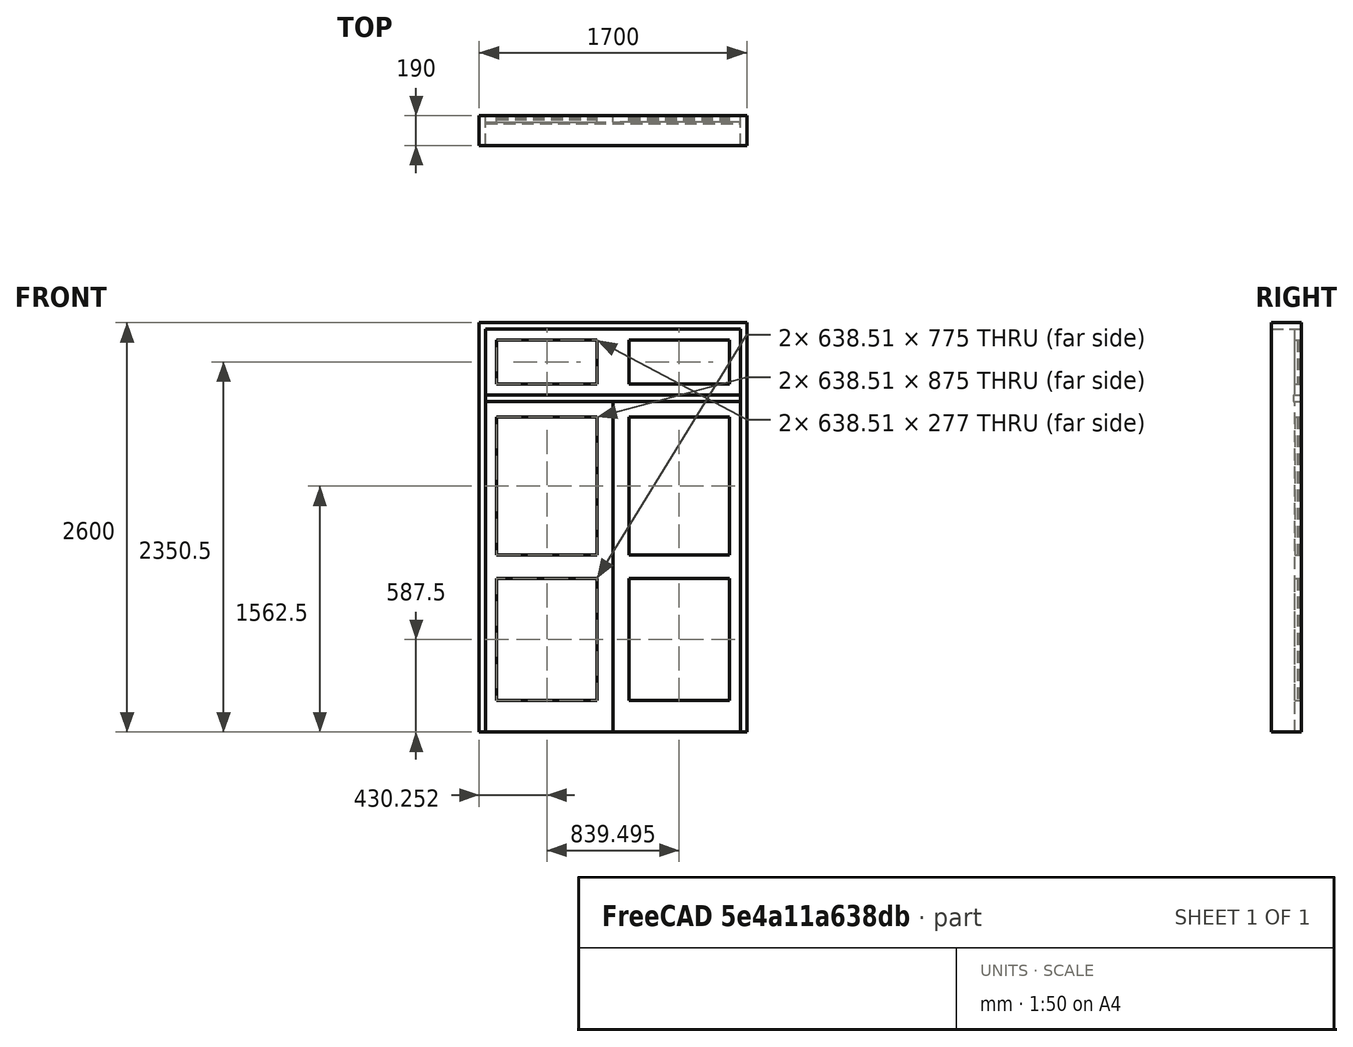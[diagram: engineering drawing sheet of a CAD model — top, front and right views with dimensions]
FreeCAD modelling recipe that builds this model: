
FCSTD DOCUMENT  (FreeCAD 0.16R6704 (Git))
Label: Double doors with glass and transom
License: CreativeCommons Attribution
LicenseURL: http://creativecommons.org/licenses/by/4.0/
objects: Sketcher::SketchObject×1, Part::FeaturePython×1
note: 2 computed .brp shape members not serialized (recipe doc carries the construction recipe); baked Part::Feature solids carry a one-line shape summary decoded from their .brp

FEATURE [Sketcher::SketchObject] Sketch179
  Placement = pos=(0,0,0) rot=(1,0,0;1.5708rad)
  sketch-geometry (50):
    g0: LineSegment StartX=0 StartY=0 StartZ=0 EndX=1700 EndY=0 EndZ=0
    g1: LineSegment StartX=1700 StartY=0 StartZ=0 EndX=1700 EndY=2600 EndZ=0
    g2: LineSegment StartX=1700 StartY=2600 StartZ=0 EndX=0 EndY=2600 EndZ=0
    g3: LineSegment StartX=0 StartY=2600 StartZ=0 EndX=0 EndY=0 EndZ=0
    g4: LineSegment StartX=40 StartY=0 StartZ=0 EndX=1660 EndY=0 EndZ=0
    g5: LineSegment StartX=1660 StartY=0 StartZ=0 EndX=1660 EndY=2560 EndZ=0
    g6: LineSegment StartX=1660 StartY=2560 StartZ=0 EndX=40 EndY=2560 EndZ=0
    g7: LineSegment StartX=40 StartY=2560 StartZ=0 EndX=40 EndY=0 EndZ=0
    g8: LineSegment StartX=111 StartY=2000 StartZ=0 EndX=749.505 EndY=2000 EndZ=0
    g9: LineSegment StartX=749.505 StartY=2000 StartZ=0 EndX=749.505 EndY=1125 EndZ=0
    g10: LineSegment StartX=749.505 StartY=1125 StartZ=0 EndX=111 EndY=1125 EndZ=0
    g11: LineSegment StartX=111 StartY=1125 StartZ=0 EndX=111 EndY=2000 EndZ=0
    g12: LineSegment StartX=111 StartY=975 StartZ=0 EndX=749.505 EndY=975 EndZ=0
    g13: LineSegment StartX=749.505 StartY=975 StartZ=0 EndX=749.505 EndY=200 EndZ=0
    g14: LineSegment StartX=749.505 StartY=200 StartZ=0 EndX=111 EndY=200 EndZ=0
    g15: LineSegment StartX=111 StartY=200 StartZ=0 EndX=111 EndY=975 EndZ=0
    g16: LineSegment [constr] StartX=-279.798 StartY=1050 StartZ=0 EndX=2204.66 EndY=1050 EndZ=0
    g17: LineSegment StartX=41 StartY=2100 StartZ=0 EndX=849.5 EndY=2100 EndZ=0
    g18: LineSegment StartX=849.5 StartY=2100 StartZ=0 EndX=849.5 EndY=1 EndZ=0
    g19: LineSegment StartX=849.5 StartY=1 StartZ=0 EndX=41 EndY=1 EndZ=0
    g20: LineSegment StartX=41 StartY=1 StartZ=0 EndX=41 EndY=2100 EndZ=0
    g21: LineSegment [constr] StartX=850 StartY=3136.34 StartZ=0 EndX=850 EndY=-186.521 EndZ=0
    g22: LineSegment StartX=1589 StartY=2000 StartZ=0 EndX=950.495 EndY=2000 EndZ=0
    g23: LineSegment StartX=950.495 StartY=2000 StartZ=0 EndX=950.495 EndY=1125 EndZ=0
    g24: LineSegment StartX=950.495 StartY=1125 StartZ=0 EndX=1589 EndY=1125 EndZ=0
    g25: LineSegment StartX=1589 StartY=1125 StartZ=0 EndX=1589 EndY=2000 EndZ=0
    g26: LineSegment StartX=1589 StartY=975 StartZ=0 EndX=950.495 EndY=975 EndZ=0
    g27: LineSegment StartX=950.495 StartY=975 StartZ=0 EndX=950.495 EndY=200 EndZ=0
    g28: LineSegment StartX=950.495 StartY=200 StartZ=0 EndX=1589 EndY=200 EndZ=0
    g29: LineSegment StartX=1589 StartY=200 StartZ=0 EndX=1589 EndY=975 EndZ=0
    g30: LineSegment StartX=1659 StartY=2100 StartZ=0 EndX=850.5 EndY=2100 EndZ=0
    g31: LineSegment StartX=850.5 StartY=2100 StartZ=0 EndX=850.5 EndY=1 EndZ=0
    g32: LineSegment StartX=850.5 StartY=1 StartZ=0 EndX=1659 EndY=1 EndZ=0
    g33: LineSegment StartX=1659 StartY=1 StartZ=0 EndX=1659 EndY=2100 EndZ=0
    g34: LineSegment StartX=41 StartY=2559 StartZ=0 EndX=1659 EndY=2559 EndZ=0
    g35: LineSegment StartX=1659 StartY=2559 StartZ=0 EndX=1659 EndY=2142 EndZ=0
    g36: LineSegment StartX=1659 StartY=2142 StartZ=0 EndX=41 EndY=2142 EndZ=0
    g37: LineSegment StartX=41 StartY=2142 StartZ=0 EndX=41 EndY=2559 EndZ=0
    g38: LineSegment StartX=111 StartY=2489 StartZ=0 EndX=749.505 EndY=2489 EndZ=0
    g39: LineSegment StartX=749.505 StartY=2489 StartZ=0 EndX=749.505 EndY=2212 EndZ=0
    g40: LineSegment StartX=749.505 StartY=2212 StartZ=0 EndX=111 EndY=2212 EndZ=0
    g41: LineSegment StartX=111 StartY=2212 StartZ=0 EndX=111 EndY=2489 EndZ=0
    g42: LineSegment StartX=950.495 StartY=2489 StartZ=0 EndX=1589 EndY=2489 EndZ=0
    g43: LineSegment StartX=1589 StartY=2489 StartZ=0 EndX=1589 EndY=2212 EndZ=0
    g44: LineSegment StartX=1589 StartY=2212 StartZ=0 EndX=950.495 EndY=2212 EndZ=0
    g45: LineSegment StartX=950.495 StartY=2212 StartZ=0 EndX=950.495 EndY=2489 EndZ=0
    g46: LineSegment StartX=41 StartY=2141 StartZ=0 EndX=1659 EndY=2141 EndZ=0
    g47: LineSegment StartX=1659 StartY=2141 StartZ=0 EndX=1659 EndY=2101 EndZ=0
    g48: LineSegment StartX=1659 StartY=2101 StartZ=0 EndX=41 EndY=2101 EndZ=0
    g49: LineSegment StartX=41 StartY=2101 StartZ=0 EndX=41 EndY=2141 EndZ=0
  constraints (143):
    c: Coincident(g0,g1)
    c: Coincident(g2,g3)
    c: Coincident(g3,g0)
    c: Horizontal(g0)
    c: Vertical(g1)
    c: Vertical(g3)
    c: Coincident(g4,g5)
    c: Coincident(g5,g6)
    c: Coincident(g6,g7)
    c: Coincident(g7,g4)
    c: Horizontal(g4)
    c: Horizontal(g6)
    c: Vertical(g5)
    c: Vertical(g7)
    c: DistanceY(g1) = 2600  'Altura do vão'
    c: DistanceX(g0) = 1700  'Largura do vão'
    c: DistanceY(g6,g2) = 40  'Altura batente superior'
    c: DistanceX(g2,g6) = 40  'Largura do batente 1'
    c: DistanceX(g4,g0) = 40  'Largura do batente 2'
    c: DistanceY(g0,g4) = 0  'Constraint21'
    c: Coincident(g0,g-1)
    c: Coincident(g8,g9)
    c: Coincident(g9,g10)
    c: Coincident(g10,g11)
    c: Coincident(g11,g8)
    c: Horizontal(g10)
    c: Vertical(g9)
    c: Vertical(g11)
    c: Coincident(g12,g13)
    c: Coincident(g13,g14)
    c: Coincident(g14,g15)
    c: Coincident(g15,g12)
    c: Horizontal(g12)
    c: Horizontal(g14)
    c: Vertical(g13)
    c: Vertical(g15)
    c: DistanceX(g9,g12) = 0
    c: DistanceY(g12,g10) = 150  'Altura do montante intermediário porta'
    c: DistanceY(g-1,g14) = 200  'Altura moldura inferior porta'
    c: DistanceY(g-1,g16) = 1050  'Altura da divisão intermediária porta'
    c: Coincident(g17,g18)  'Constraint46'
    c: Coincident(g18,g19)  'Constraint45'
    c: Coincident(g19,g20)  'Constraint43'
    c: Horizontal(g17)
    c: Horizontal(g19)
    c: Vertical(g18)
    c: Vertical(g20)
    c: DistanceY(g4,g18) = 1
    c: DistanceX(g6,g17) = 1
    c: Coincident(g22,g23)  'Constraint57'
    c: Coincident(g23,g24)  'Constraint55'
    c: Coincident(g24,g25)  'Constraint54'
    c: Coincident(g25,g22)
    c: Horizontal(g24)
    c: Vertical(g23)
    c: Vertical(g25)
    c: Coincident(g26,g27)
    c: Coincident(g27,g28)
    c: Coincident(g28,g29)
    c: Coincident(g29,g26)
    c: Horizontal(g26)
    c: Horizontal(g28)
    c: Vertical(g27)
    c: Vertical(g29)
    c: Coincident(g30,g31)
    c: Coincident(g31,g32)
    c: Coincident(g32,g33)
    c: Horizontal(g30)
    c: Horizontal(g32)
    c: Vertical(g31)
    c: Vertical(g33)
    c: DistanceX(g30,g5) = 1
    c: Symmetric(g17,g30,g21)
    c: DistanceX(g17,g30) = 1
    c: DistanceY(g9,g23) = 0
    c: DistanceY(g18,g31) = 0
    c: DistanceX(g24,g26) = 0
    c: Coincident(g30,g33)
    c: DistanceY(g8,g17) = 100  'Altura moldura superior porta'
    c: Coincident(g34,g35)  'Constraint94'
    c: Coincident(g35,g36)  'Constraint93'
    c: Coincident(g36,g37)  'Constraint92'
    c: Coincident(g37,g34)  'Constraint91'
    c: Horizontal(g34)  'Constraint90'
    c: Horizontal(g36)
    c: Vertical(g35)
    c: Vertical(g37)
    c: Coincident(g38,g39)
    c: Coincident(g39,g40)
    c: Coincident(g40,g41)
    c: Coincident(g41,g38)
    c: Horizontal(g38)
    c: Horizontal(g40)
    c: Vertical(g39)
    c: Vertical(g41)
    c: Coincident(g42,g43)
    c: Coincident(g43,g44)
    c: Coincident(g44,g45)
    c: Coincident(g45,g42)
    c: Horizontal(g42)
    c: Horizontal(g44)
    c: Vertical(g43)
    c: Vertical(g45)
    c: Coincident(g46,g47)
    c: Coincident(g47,g48)
    c: Coincident(g48,g49)
    c: Coincident(g49,g46)
    c: Horizontal(g46)
    c: Horizontal(g48)
    c: Vertical(g47)
    c: Vertical(g49)
    c: DistanceX(g17,g48) = 0
    c: DistanceX(g47,g30) = 0
    c: DistanceY(g17,g48) = 1  'Constraint129'
    c: DistanceY(g47,g46) = 40  'Batente bandeira'
    c: DistanceY(g46,g35) = 1  'Constraint127'
    c: DistanceX(g35,g46) = 0  'Constraint126'
    c: DistanceX(g46,g36) = 0
    c: DistanceY(g34,g6) = 1
    c: DistanceX(g40,g8) = 0
    c: DistanceY(g36,g40) = 70  'Moldura inferior bandeira'
    c: DistanceX(g39,g8) = 0  'Constraint135'
    c: DistanceX(g22,g44) = 0
    c: DistanceY(g39,g44) = 0
    c: DistanceX(g43,g22) = 0
    c: DistanceY(g38,g42) = 0
    c: DistanceY(g38,g34) = 70  'Altura moldura superior bandeira'
    c: DistanceY(g-1,g17) = 2100  'Altura porta'
    c: Coincident(g17,g20)
    c: DistanceY(g27,g13) = 0
    c: DistanceX(g17,g8) = 70  'Largura montante vertica porta 1'
    c: Symmetric(g-1,g0,g21)
    c: DistanceY(g8,g22) = 0
    c: DistanceY(g12,g26) = 0
    c: DistanceX(g23,g26) = 0
    c: DistanceX(g10,g12) = 0
    c: Symmetric(g10,g12,g16)
    c: Symmetric(g38,g42,g21)
    c: Symmetric(g38,g42,g21)
    c: Coincident(g2,g1)
    c: Horizontal(g2)
    c: Horizontal(g8)
    c: Horizontal(g22)
FEATURE [Part::FeaturePython] Window112  label="Double doors with glass and transom"  # WARN: FeaturePython — macro-defined, semantics opaque (R4)
  Base = -> Sketch179
  Height = 2100
  HoleDepth = 0
  MoveWithHost = true
  Normal = (0,1,0)
  Preset = 6
  Role = 1
  Width = 900
  WindowParts = BATENTE | Frame | Wire0,Wire1 | 190.0 | 0.0 | PORTA 1 | Frame | Wire2,Wire3,Wire4 | 40.0 | 150.0 | PORTA 2 | Frame | Wire5,Wire6,Wire7 | 40.0 | 150.0 | BATENTE BANDEIRA | Frame | Wire11 | 50.0 | 140.0 | BANDEIRA | Frame | Wire10,Wire9,Wire8 | 40.0 | 150.0 | VIDRO 1 BANDEIRA | Glass panel | Wire9 | 10.0 | 165.0 | VIDRO 2 BANDEIRA | Glass panel | Wire10 | 10.0 | 165.0 | VIDRO SUPERIOR PORTA 1 | Glass panel | Wire2 | 10.0 | 165.0 | VIDRO SUPERIOR PORTA 2 | Glass panel | Wire5 | 10.0 | 165.0 | VIDRO INFERIOR PORTA 1 | Glass panel | Wire3 | 10.0 | 165.0 | VIDRO INFERIOR PORTA 2 | Glass panel | Wire6 | 10.0 | 165.0
